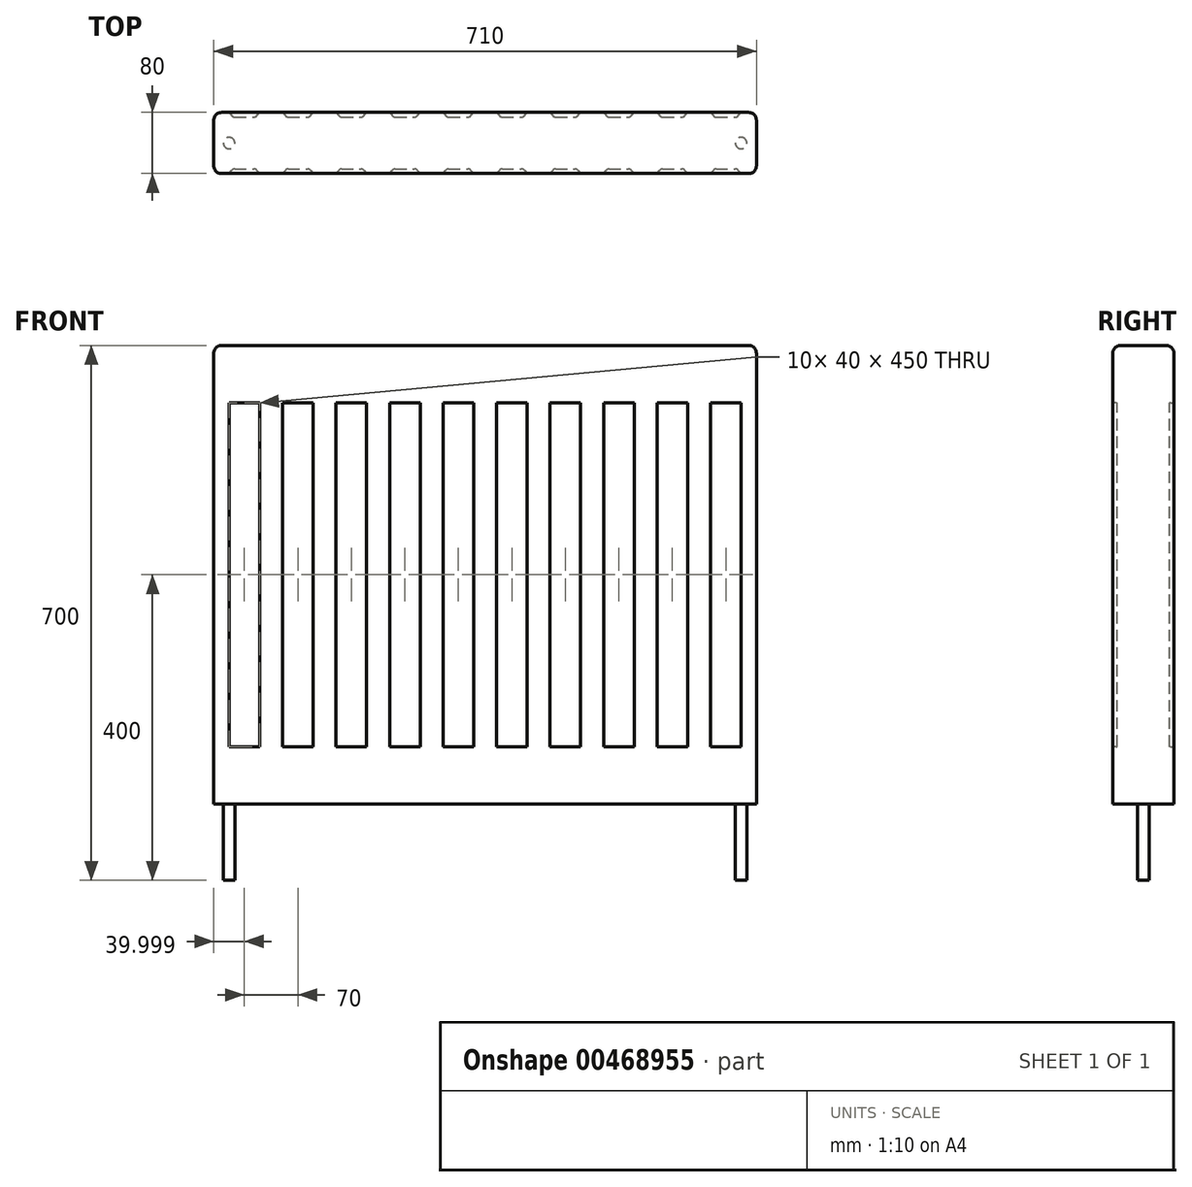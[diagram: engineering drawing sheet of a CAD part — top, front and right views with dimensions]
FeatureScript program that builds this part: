
annotation { "Feature Type Name" : "Feature", "Feature Type Description" : "" }
export const myFeature = defineFeature(function(context is Context, id is Id, definition is map)
    precondition{}
    {
        {
            var Q0;
            Q0=qCreatedBy(makeId("Top.planeOp"),FACE);
            var sketch = newSketch(context, id + "F0", { "sketchPlane" : qUnion([Q0])});
            skLineSegment(sketch, "E0.bottom", {"start": v(-345.66, -18.68) * mm, "end": v(364.34, -18.68) * mm});
            skLineSegment(sketch, "E0.top", {"start": v(-345.66, -98.68) * mm, "end": v(364.34, -98.68) * mm});
            skLineSegment(sketch, "E0.left", {"start": v(-345.66, -18.68) * mm, "end": v(-345.66, -98.68) * mm});
            skLineSegment(sketch, "E0.right", {"start": v(364.34, -18.68) * mm, "end": v(364.34, -98.68) * mm});
            skSolve(sketch);
        }
        {
            var Q0;
            Q0=makeQuery(id+"F0.imprint","IMPRINT",FACE,{"disambiguationData":[TD([[makeQuery(id+"F0.imprint","IMPRINT",EDGE,{"derivedFrom":sQuery(id+"F0.wireOp",EDGE,"E0.bottom")}),-1.0]])]});
            extrude(context, id + "F1", {"entities" : qUnion([Q0]), "endBound" : BoundingType.SYMMETRIC, "depth" : 600 * mm});
        }
        {
            var Q0;
            Q0=makeQuery(id+"F1.opExtrude","CAP_FACE",FACE,{"disambiguationData":[OSD([sQuery(id+"F0.wireOp",EDGE,"E0.bottom"),sQuery(id+"F0.wireOp",EDGE,"E0.top"),sQuery(id+"F0.wireOp",EDGE,"E0.left"),sQuery(id+"F0.wireOp",EDGE,"E0.right")])],"isStart":true});
            var sketch = newSketch(context, id + "F2", { "sketchPlane" : qUnion([Q0])});
            skCircle(sketch, "E1", {"center": v(-325.66, 58.68) * mm, "radius": 7.5 * mm});
            skPoint(sketch, "E1.centerSnap0", {"position": v(-345.66, 58.68) * mm});
            skCircle(sketch, "E2", {"center": v(344.34, 58.68) * mm, "radius": 7.5 * mm});
            skPoint(sketch, "E2.centerSnap0", {"position": v(364.34, 58.68) * mm});
            skSolve(sketch);
        }
        {
            var Q0;
            Q0=makeQuery(id+"F2.imprint","IMPRINT",FACE,{"disambiguationData":[TD([[makeQuery(id+"F2.imprint","IMPRINT",EDGE,{"derivedFrom":sQuery(id+"F2.wireOp",EDGE,"E2")}),1.0]])]});
            var Q1;
            Q1=makeQuery(id+"F2.imprint","IMPRINT",FACE,{"disambiguationData":[TD([[makeQuery(id+"F2.imprint","IMPRINT",EDGE,{"derivedFrom":sQuery(id+"F2.wireOp",EDGE,"E1")}),1.0]])]});
            extrude(context, id + "F3", {"entities" : qUnion([Q0, Q1]), "operationType" : NewBodyOperationType.ADD, "depth" : 100 * mm});
        }
        {
            var Q0;
            Q0=qCreatedBy(makeId("Top.planeOp"),FACE);
            var sketch = newSketch(context, id + "F4", { "sketchPlane" : qUnion([Q0])});
            skLineSegment(sketch, "E3", {"start": v(-325.66, -18.68) * mm, "end": v(-322.12, -22.9) * mm});
            skLineSegment(sketch, "E4", {"start": v(-318.3, -24.68) * mm, "end": v(-293.03, -24.68) * mm});
            skLineSegment(sketch, "E5", {"start": v(-289.2, -22.9) * mm, "end": v(-285.66, -18.68) * mm});
            skPoint(sketch, "E6.visualSharp", {"position": v(-320.63, -24.68) * mm});
            skArc(sketch, "E6.filletArc", {"start": v(-322.12, -22.9) * mm, "mid": v(-320.4, -24.22) * mm, "end": v(-318.3, -24.68) * mm});
            skPoint(sketch, "E7.visualSharp", {"position": v(-290.7, -24.68) * mm});
            skArc(sketch, "E7.filletArc", {"start": v(-293.03, -24.68) * mm, "mid": v(-290.91, -24.22) * mm, "end": v(-289.2, -22.9) * mm});
            skLineSegment(sketch, "E8.1.0.0", {"start": v(-255.66, -18.68) * mm, "end": v(-252.12, -22.9) * mm});
            skArc(sketch, "E8.1.0.1", {"start": v(-252.12, -22.9) * mm, "mid": v(-250.4, -24.22) * mm, "end": v(-248.3, -24.68) * mm});
            skLineSegment(sketch, "E8.1.0.2", {"start": v(-248.3, -24.68) * mm, "end": v(-223.03, -24.68) * mm});
            skArc(sketch, "E8.1.0.3", {"start": v(-223.03, -24.68) * mm, "mid": v(-220.91, -24.22) * mm, "end": v(-219.2, -22.9) * mm});
            skLineSegment(sketch, "E8.1.0.4", {"start": v(-219.2, -22.9) * mm, "end": v(-215.66, -18.68) * mm});
            skLineSegment(sketch, "E8.2.0.0", {"start": v(-185.66, -18.68) * mm, "end": v(-182.12, -22.9) * mm});
            skArc(sketch, "E8.2.0.1", {"start": v(-182.12, -22.9) * mm, "mid": v(-180.4, -24.22) * mm, "end": v(-178.3, -24.68) * mm});
            skLineSegment(sketch, "E8.2.0.2", {"start": v(-178.3, -24.68) * mm, "end": v(-153.03, -24.68) * mm});
            skArc(sketch, "E8.2.0.3", {"start": v(-153.03, -24.68) * mm, "mid": v(-150.91, -24.22) * mm, "end": v(-149.2, -22.9) * mm});
            skLineSegment(sketch, "E8.2.0.4", {"start": v(-149.2, -22.9) * mm, "end": v(-145.66, -18.68) * mm});
            skLineSegment(sketch, "E8.3.0.0", {"start": v(-115.66, -18.68) * mm, "end": v(-112.12, -22.9) * mm});
            skArc(sketch, "E8.3.0.1", {"start": v(-112.12, -22.9) * mm, "mid": v(-110.4, -24.22) * mm, "end": v(-108.3, -24.68) * mm});
            skLineSegment(sketch, "E8.3.0.2", {"start": v(-108.3, -24.68) * mm, "end": v(-83.03, -24.68) * mm});
            skArc(sketch, "E8.3.0.3", {"start": v(-83.03, -24.68) * mm, "mid": v(-80.91, -24.22) * mm, "end": v(-79.2, -22.9) * mm});
            skLineSegment(sketch, "E8.3.0.4", {"start": v(-79.2, -22.9) * mm, "end": v(-75.66, -18.68) * mm});
            skLineSegment(sketch, "E8.4.0.0", {"start": v(-45.66, -18.68) * mm, "end": v(-42.12, -22.9) * mm});
            skArc(sketch, "E8.4.0.1", {"start": v(-42.12, -22.9) * mm, "mid": v(-40.4, -24.22) * mm, "end": v(-38.3, -24.68) * mm});
            skLineSegment(sketch, "E8.4.0.2", {"start": v(-38.3, -24.68) * mm, "end": v(-13.03, -24.68) * mm});
            skArc(sketch, "E8.4.0.3", {"start": v(-13.03, -24.68) * mm, "mid": v(-10.91, -24.22) * mm, "end": v(-9.2, -22.9) * mm});
            skLineSegment(sketch, "E8.4.0.4", {"start": v(-9.2, -22.9) * mm, "end": v(-5.66, -18.68) * mm});
            skLineSegment(sketch, "E8.5.0.0", {"start": v(24.34, -18.68) * mm, "end": v(27.88, -22.9) * mm});
            skArc(sketch, "E8.5.0.1", {"start": v(27.88, -22.9) * mm, "mid": v(29.6, -24.22) * mm, "end": v(31.7, -24.68) * mm});
            skLineSegment(sketch, "E8.5.0.2", {"start": v(31.7, -24.68) * mm, "end": v(56.97, -24.68) * mm});
            skArc(sketch, "E8.5.0.3", {"start": v(56.97, -24.68) * mm, "mid": v(59.09, -24.22) * mm, "end": v(60.8, -22.9) * mm});
            skLineSegment(sketch, "E8.5.0.4", {"start": v(60.8, -22.9) * mm, "end": v(64.34, -18.68) * mm});
            skLineSegment(sketch, "E8.6.0.0", {"start": v(94.34, -18.68) * mm, "end": v(97.88, -22.9) * mm});
            skArc(sketch, "E8.6.0.1", {"start": v(97.88, -22.9) * mm, "mid": v(99.6, -24.22) * mm, "end": v(101.7, -24.68) * mm});
            skLineSegment(sketch, "E8.6.0.2", {"start": v(101.7, -24.68) * mm, "end": v(126.97, -24.68) * mm});
            skArc(sketch, "E8.6.0.3", {"start": v(126.97, -24.68) * mm, "mid": v(129.09, -24.22) * mm, "end": v(130.8, -22.9) * mm});
            skLineSegment(sketch, "E8.6.0.4", {"start": v(130.8, -22.9) * mm, "end": v(134.34, -18.68) * mm});
            skLineSegment(sketch, "E8.7.0.0", {"start": v(164.34, -18.68) * mm, "end": v(167.88, -22.9) * mm});
            skArc(sketch, "E8.7.0.1", {"start": v(167.88, -22.9) * mm, "mid": v(169.6, -24.22) * mm, "end": v(171.7, -24.68) * mm});
            skLineSegment(sketch, "E8.7.0.2", {"start": v(171.7, -24.68) * mm, "end": v(196.97, -24.68) * mm});
            skArc(sketch, "E8.7.0.3", {"start": v(196.97, -24.68) * mm, "mid": v(199.09, -24.22) * mm, "end": v(200.8, -22.9) * mm});
            skLineSegment(sketch, "E8.7.0.4", {"start": v(200.8, -22.9) * mm, "end": v(204.34, -18.68) * mm});
            skLineSegment(sketch, "E8.8.0.0", {"start": v(234.34, -18.68) * mm, "end": v(237.88, -22.9) * mm});
            skArc(sketch, "E8.8.0.1", {"start": v(237.88, -22.9) * mm, "mid": v(239.6, -24.22) * mm, "end": v(241.7, -24.68) * mm});
            skLineSegment(sketch, "E8.8.0.2", {"start": v(241.7, -24.68) * mm, "end": v(266.97, -24.68) * mm});
            skArc(sketch, "E8.8.0.3", {"start": v(266.97, -24.68) * mm, "mid": v(269.09, -24.22) * mm, "end": v(270.8, -22.9) * mm});
            skLineSegment(sketch, "E8.8.0.4", {"start": v(270.8, -22.9) * mm, "end": v(274.34, -18.68) * mm});
            skLineSegment(sketch, "E8.9.0.0", {"start": v(304.34, -18.68) * mm, "end": v(307.88, -22.9) * mm});
            skArc(sketch, "E8.9.0.1", {"start": v(307.88, -22.9) * mm, "mid": v(309.6, -24.22) * mm, "end": v(311.7, -24.68) * mm});
            skLineSegment(sketch, "E8.9.0.2", {"start": v(311.7, -24.68) * mm, "end": v(336.97, -24.68) * mm});
            skArc(sketch, "E8.9.0.3", {"start": v(336.97, -24.68) * mm, "mid": v(339.09, -24.22) * mm, "end": v(340.8, -22.9) * mm});
            skLineSegment(sketch, "E8.9.0.4", {"start": v(340.8, -22.9) * mm, "end": v(344.34, -18.68) * mm});
            skLineSegment(sketch, "E8.direction1", {"start": v(-322.12, -22.9) * mm, "end": v(-252.12, -22.9) * mm, "construction": true});
            skLineSegment(sketch, "E9", {"start": v(-345.66, -58.68) * mm, "end": v(364.34, -58.68) * mm, "construction": true});
            skArc(sketch, "E10.MirrorCS", {"start": v(-322.12, -94.47) * mm, "mid": v(-320.4, -93.15) * mm, "end": v(-318.3, -92.68) * mm});
            skLineSegment(sketch, "E11.MirrorCS", {"start": v(-325.66, -98.68) * mm, "end": v(-322.12, -94.47) * mm});
            skLineSegment(sketch, "E12.MirrorCS", {"start": v(-289.2, -94.47) * mm, "end": v(-285.66, -98.68) * mm});
            skLineSegment(sketch, "E13.MirrorCS", {"start": v(-255.66, -98.68) * mm, "end": v(-252.12, -94.47) * mm});
            skArc(sketch, "E14.MirrorCS", {"start": v(-293.03, -92.68) * mm, "mid": v(-290.91, -93.15) * mm, "end": v(-289.2, -94.47) * mm});
            skArc(sketch, "E15.MirrorCS", {"start": v(-252.12, -94.47) * mm, "mid": v(-250.4, -93.15) * mm, "end": v(-248.3, -92.68) * mm});
            skArc(sketch, "E16.MirrorCS", {"start": v(196.97, -92.68) * mm, "mid": v(199.09, -93.15) * mm, "end": v(200.8, -94.47) * mm});
            skLineSegment(sketch, "E17.MirrorCS", {"start": v(-115.66, -98.68) * mm, "end": v(-112.12, -94.47) * mm});
            skLineSegment(sketch, "E18.MirrorCS", {"start": v(-149.2, -94.47) * mm, "end": v(-145.66, -98.68) * mm});
            skArc(sketch, "E19.MirrorCS", {"start": v(-153.03, -92.68) * mm, "mid": v(-150.91, -93.15) * mm, "end": v(-149.2, -94.47) * mm});
            skLineSegment(sketch, "E20.MirrorCS", {"start": v(304.34, -98.68) * mm, "end": v(307.88, -94.47) * mm});
            skLineSegment(sketch, "E21.MirrorCS", {"start": v(-45.66, -98.68) * mm, "end": v(-42.12, -94.47) * mm});
            skArc(sketch, "E22.MirrorCS", {"start": v(167.88, -94.47) * mm, "mid": v(169.6, -93.15) * mm, "end": v(171.7, -92.68) * mm});
            skLineSegment(sketch, "E23.MirrorCS", {"start": v(60.8, -94.47) * mm, "end": v(64.34, -98.68) * mm});
            skArc(sketch, "E24.MirrorCS", {"start": v(266.97, -92.68) * mm, "mid": v(269.09, -93.15) * mm, "end": v(270.8, -94.47) * mm});
            skArc(sketch, "E25.MirrorCS", {"start": v(307.88, -94.47) * mm, "mid": v(309.6, -93.15) * mm, "end": v(311.7, -92.68) * mm});
            skArc(sketch, "E26.MirrorCS", {"start": v(-42.12, -94.47) * mm, "mid": v(-40.4, -93.15) * mm, "end": v(-38.3, -92.68) * mm});
            skLineSegment(sketch, "E27.MirrorCS", {"start": v(94.34, -98.68) * mm, "end": v(97.88, -94.47) * mm});
            skLineSegment(sketch, "E28.MirrorCS", {"start": v(-79.2, -94.47) * mm, "end": v(-75.66, -98.68) * mm});
            skLineSegment(sketch, "E29.MirrorCS", {"start": v(164.34, -98.68) * mm, "end": v(167.88, -94.47) * mm});
            skArc(sketch, "E30.MirrorCS", {"start": v(27.88, -94.47) * mm, "mid": v(29.6, -93.15) * mm, "end": v(31.7, -92.68) * mm});
            skArc(sketch, "E31.MirrorCS", {"start": v(-83.03, -92.68) * mm, "mid": v(-80.91, -93.15) * mm, "end": v(-79.2, -94.47) * mm});
            skLineSegment(sketch, "E32.MirrorCS", {"start": v(130.8, -94.47) * mm, "end": v(134.34, -98.68) * mm});
            skLineSegment(sketch, "E33.MirrorCS", {"start": v(24.34, -98.68) * mm, "end": v(27.88, -94.47) * mm});
            skArc(sketch, "E34.MirrorCS", {"start": v(237.88, -94.47) * mm, "mid": v(239.6, -93.15) * mm, "end": v(241.7, -92.68) * mm});
            skArc(sketch, "E35.MirrorCS", {"start": v(-182.12, -94.47) * mm, "mid": v(-180.4, -93.15) * mm, "end": v(-178.3, -92.68) * mm});
            skArc(sketch, "E36.MirrorCS", {"start": v(56.97, -92.68) * mm, "mid": v(59.09, -93.15) * mm, "end": v(60.8, -94.47) * mm});
            skLineSegment(sketch, "E37.MirrorCS", {"start": v(270.8, -94.47) * mm, "end": v(274.34, -98.68) * mm});
            skArc(sketch, "E38.MirrorCS", {"start": v(126.97, -92.68) * mm, "mid": v(129.09, -93.15) * mm, "end": v(130.8, -94.47) * mm});
            skLineSegment(sketch, "E39.MirrorCS", {"start": v(-9.2, -94.47) * mm, "end": v(-5.66, -98.68) * mm});
            skLineSegment(sketch, "E40.MirrorCS", {"start": v(234.34, -98.68) * mm, "end": v(237.88, -94.47) * mm});
            skLineSegment(sketch, "E41.MirrorCS", {"start": v(340.8, -94.47) * mm, "end": v(344.34, -98.68) * mm});
            skLineSegment(sketch, "E42.MirrorCS", {"start": v(-185.66, -98.68) * mm, "end": v(-182.12, -94.47) * mm});
            skLineSegment(sketch, "E43.MirrorCS", {"start": v(-219.2, -94.47) * mm, "end": v(-215.66, -98.68) * mm});
            skArc(sketch, "E44.MirrorCS", {"start": v(-223.03, -92.68) * mm, "mid": v(-220.91, -93.15) * mm, "end": v(-219.2, -94.47) * mm});
            skArc(sketch, "E45.MirrorCS", {"start": v(-13.03, -92.68) * mm, "mid": v(-10.91, -93.15) * mm, "end": v(-9.2, -94.47) * mm});
            skLineSegment(sketch, "E46.MirrorCS", {"start": v(200.8, -94.47) * mm, "end": v(204.34, -98.68) * mm});
            skArc(sketch, "E47.MirrorCS", {"start": v(97.88, -94.47) * mm, "mid": v(99.6, -93.15) * mm, "end": v(101.7, -92.68) * mm});
            skArc(sketch, "E48.MirrorCS", {"start": v(-112.12, -94.47) * mm, "mid": v(-110.4, -93.15) * mm, "end": v(-108.3, -92.68) * mm});
            skArc(sketch, "E49.MirrorCS", {"start": v(336.97, -92.68) * mm, "mid": v(339.09, -93.15) * mm, "end": v(340.8, -94.47) * mm});
            skLineSegment(sketch, "E50.MirrorCS", {"start": v(-318.3, -92.68) * mm, "end": v(-293.03, -92.68) * mm});
            skLineSegment(sketch, "E51.MirrorCS", {"start": v(-38.3, -92.68) * mm, "end": v(-13.03, -92.68) * mm});
            skLineSegment(sketch, "E52.MirrorCS", {"start": v(311.7, -92.68) * mm, "end": v(336.97, -92.68) * mm});
            skLineSegment(sketch, "E53.MirrorCS", {"start": v(101.7, -92.68) * mm, "end": v(126.97, -92.68) * mm});
            skLineSegment(sketch, "E54.MirrorCS", {"start": v(31.7, -92.68) * mm, "end": v(56.97, -92.68) * mm});
            skLineSegment(sketch, "E55.MirrorCS", {"start": v(171.7, -92.68) * mm, "end": v(196.97, -92.68) * mm});
            skPoint(sketch, "E56.MirrorP", {"position": v(-290.7, -92.68) * mm});
            skLineSegment(sketch, "E57.MirrorCS", {"start": v(241.7, -92.68) * mm, "end": v(266.97, -92.68) * mm});
            skLineSegment(sketch, "E58.MirrorCS", {"start": v(-322.12, -94.47) * mm, "end": v(-252.12, -94.47) * mm, "construction": true});
            skLineSegment(sketch, "E59.MirrorCS", {"start": v(-178.3, -92.68) * mm, "end": v(-153.03, -92.68) * mm});
            skLineSegment(sketch, "E60.MirrorCS", {"start": v(-108.3, -92.68) * mm, "end": v(-83.03, -92.68) * mm});
            skPoint(sketch, "E61.MirrorP", {"position": v(-320.63, -92.68) * mm});
            skLineSegment(sketch, "E62.MirrorCS", {"start": v(-248.3, -92.68) * mm, "end": v(-223.03, -92.68) * mm});
            skLineSegment(sketch, "E63", {"start": v(-325.66, -18.68) * mm, "end": v(-285.66, -18.68) * mm});
            skLineSegment(sketch, "E64", {"start": v(-255.66, -18.68) * mm, "end": v(-215.66, -18.68) * mm});
            skLineSegment(sketch, "E65", {"start": v(-185.66, -18.68) * mm, "end": v(-145.66, -18.68) * mm});
            skLineSegment(sketch, "E66", {"start": v(-115.66, -18.68) * mm, "end": v(-75.66, -18.68) * mm});
            skLineSegment(sketch, "E67", {"start": v(-45.66, -18.68) * mm, "end": v(-5.66, -18.68) * mm});
            skLineSegment(sketch, "E68", {"start": v(24.34, -18.68) * mm, "end": v(64.34, -18.68) * mm});
            skLineSegment(sketch, "E69", {"start": v(94.34, -18.68) * mm, "end": v(134.34, -18.68) * mm});
            skLineSegment(sketch, "E70", {"start": v(164.34, -18.68) * mm, "end": v(204.34, -18.68) * mm});
            skLineSegment(sketch, "E71", {"start": v(234.34, -18.68) * mm, "end": v(274.34, -18.68) * mm});
            skLineSegment(sketch, "E72", {"start": v(304.34, -18.68) * mm, "end": v(344.34, -18.68) * mm});
            skLineSegment(sketch, "E73", {"start": v(344.34, -98.68) * mm, "end": v(304.34, -98.68) * mm});
            skLineSegment(sketch, "E74", {"start": v(274.34, -98.68) * mm, "end": v(234.34, -98.68) * mm});
            skLineSegment(sketch, "E75", {"start": v(204.34, -98.68) * mm, "end": v(164.34, -98.68) * mm});
            skLineSegment(sketch, "E76", {"start": v(134.34, -98.68) * mm, "end": v(94.34, -98.68) * mm});
            skLineSegment(sketch, "E77", {"start": v(64.34, -98.68) * mm, "end": v(24.34, -98.68) * mm});
            skLineSegment(sketch, "E78", {"start": v(-5.66, -98.68) * mm, "end": v(-45.66, -98.68) * mm});
            skLineSegment(sketch, "E79", {"start": v(-75.66, -98.68) * mm, "end": v(-115.66, -98.68) * mm});
            skLineSegment(sketch, "E80", {"start": v(-145.66, -98.68) * mm, "end": v(-185.66, -98.68) * mm});
            skLineSegment(sketch, "E81", {"start": v(-215.66, -98.68) * mm, "end": v(-255.66, -98.68) * mm});
            skLineSegment(sketch, "E82", {"start": v(-285.66, -98.68) * mm, "end": v(-325.66, -98.68) * mm});
            skSolve(sketch);
        }
        {
            var Q0;
            Q0 = qSketchRegion(id + "F4", true);
            extrude(context, id + "F5", {"entities" : qUnion([Q0]), "operationType" : NewBodyOperationType.REMOVE, "endBound" : BoundingType.SYMMETRIC, "oppositeDirection" : true, "depth" : 450 * mm});
        }
        {
            var Q0;
            Q0=makeQuery(id+"F1.opExtrude","SWEPT_EDGE",EDGE,{"disambiguationData":[OSD([sQuery(id+"F0.wireOp",EDGE,"E0.top"),sQuery(id+"F0.wireOp",EDGE,"E0.left")])]});
            var Q1;
            Q1=makeQuery(id+"F1.opExtrude","SWEPT_EDGE",EDGE,{"disambiguationData":[OSD([sQuery(id+"F0.wireOp",EDGE,"E0.bottom"),sQuery(id+"F0.wireOp",EDGE,"E0.left")])]});
            var Q2;
            Q2=makeQuery(id+"F1.opExtrude","SWEPT_EDGE",EDGE,{"disambiguationData":[OSD([sQuery(id+"F0.wireOp",EDGE,"E0.top"),sQuery(id+"F0.wireOp",EDGE,"E0.right")])]});
            var Q3;
            Q3=makeQuery(id+"F1.opExtrude","SWEPT_EDGE",EDGE,{"disambiguationData":[OSD([sQuery(id+"F0.wireOp",EDGE,"E0.bottom"),sQuery(id+"F0.wireOp",EDGE,"E0.right")])]});
            var Q4;
            Q4=makeQuery(id+"F1.opExtrude","CAP_EDGE",EDGE,{"disambiguationData":[OSD([sQuery(id+"F0.wireOp",EDGE,"E0.top")])],"isStart":false});
            var Q5;
            Q5=makeQuery(id+"F1.opExtrude","CAP_EDGE",EDGE,{"disambiguationData":[OSD([sQuery(id+"F0.wireOp",EDGE,"E0.bottom")])],"isStart":false});
            var Q6;
            Q6=makeQuery(id+"F1.opExtrude","CAP_EDGE",EDGE,{"disambiguationData":[OSD([sQuery(id+"F0.wireOp",EDGE,"E0.right")])],"isStart":false});
            var Q7;
            Q7=makeQuery(id+"F1.opExtrude","CAP_EDGE",EDGE,{"disambiguationData":[OSD([sQuery(id+"F0.wireOp",EDGE,"E0.left")])],"isStart":false});
            fillet(context, id + "F6", {"entities" : qUnion([Q0, Q1, Q2, Q3, Q4, Q5, Q6, Q7]), "radius" : 10 * mm, "tangentPropagation" : true, "allowEdgeOverflow" : false});
        }
    });
